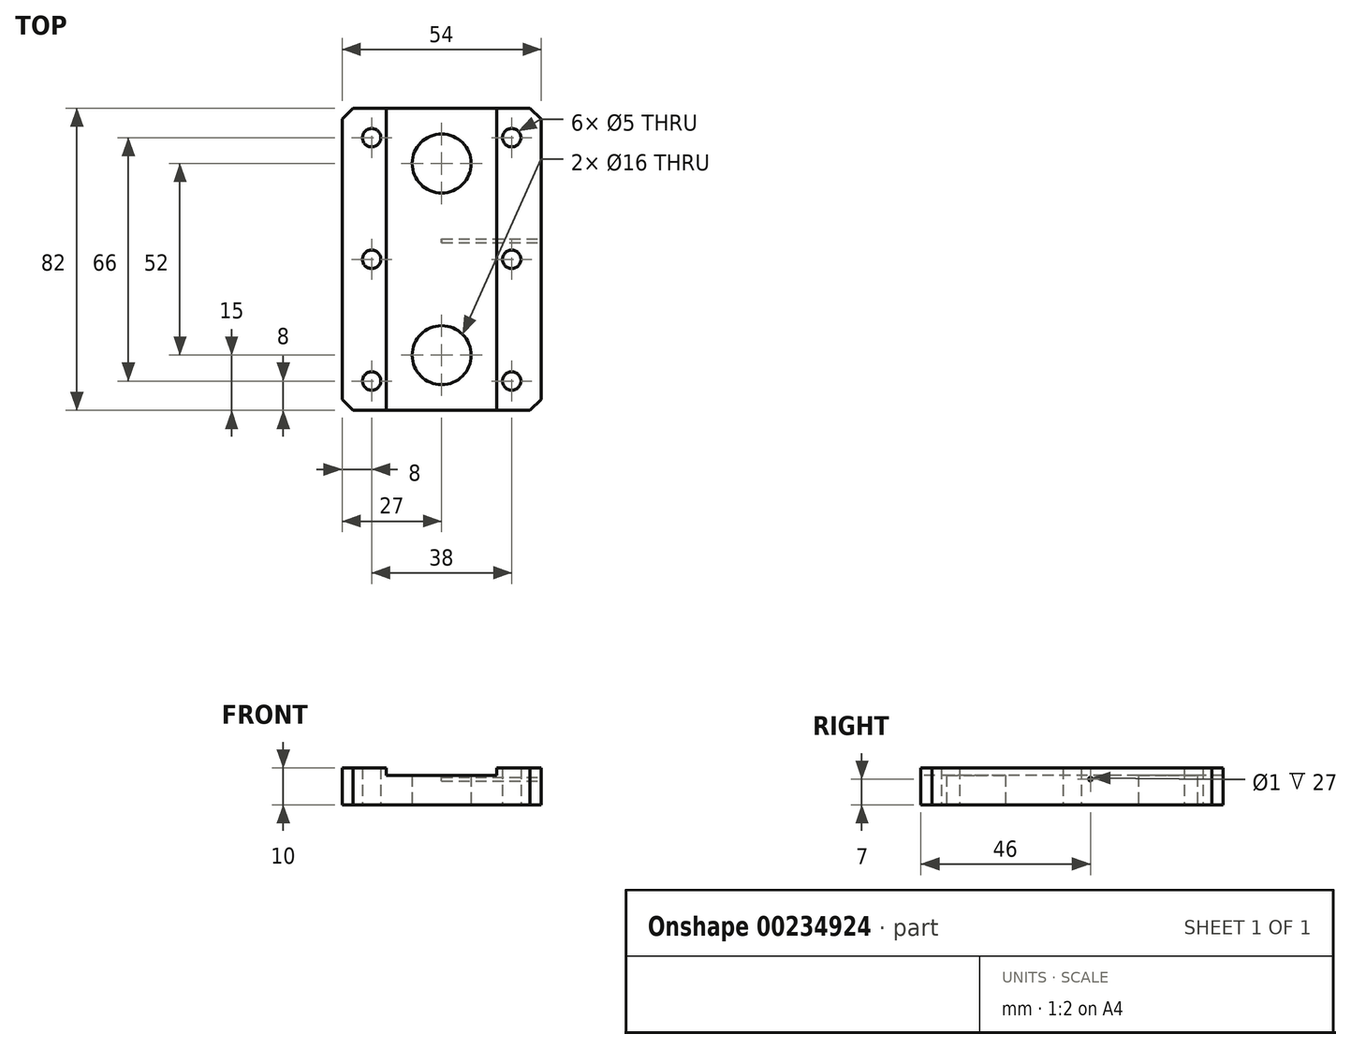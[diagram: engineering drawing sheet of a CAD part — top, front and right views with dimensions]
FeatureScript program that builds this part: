
annotation { "Feature Type Name" : "Feature", "Feature Type Description" : "" }
export const myFeature = defineFeature(function(context is Context, id is Id, definition is map)
    precondition{}
    {
        {
            var Q0;
            Q0=qCreatedBy(makeId("Top.planeOp"),FACE);
            var sketch = newSketch(context, id + "F0", { "sketchPlane" : qUnion([Q0])});
            skLineSegment(sketch, "E0.bottom", {"start": v(27, 41) * mm, "end": v(-27, 41) * mm});
            skLineSegment(sketch, "E0.top", {"start": v(27, -41) * mm, "end": v(-27, -41) * mm});
            skLineSegment(sketch, "E0.left", {"start": v(27, 41) * mm, "end": v(27, -41) * mm});
            skLineSegment(sketch, "E0.right", {"start": v(-27, 41) * mm, "end": v(-27, -41) * mm});
            skPoint(sketch, "E0.middle", {"position": v(0, 0) * mm});
            skLineSegment(sketch, "E1", {"start": v(0, 41) * mm, "end": v(0, -41) * mm, "construction": true});
            skLineSegment(sketch, "E2", {"start": v(-27, 0) * mm, "end": v(27, 0) * mm, "construction": true});
            skCircle(sketch, "E3", {"center": v(0, -26) * mm, "radius": 8 * mm});
            skCircle(sketch, "E4", {"center": v(0, 26) * mm, "radius": 8 * mm});
            skLineSegment(sketch, "E5", {"start": v(-19, 41) * mm, "end": v(-19, -41) * mm, "construction": true});
            skCircle(sketch, "E6", {"center": v(-19, 0) * mm, "radius": 2.5 * mm});
            skCircle(sketch, "E7", {"center": v(-19, 33) * mm, "radius": 2.5 * mm});
            skCircle(sketch, "E8", {"center": v(-19, -33) * mm, "radius": 2.5 * mm});
            skCircle(sketch, "E9.MirrorC", {"center": v(19, -33) * mm, "radius": 2.5 * mm});
            skCircle(sketch, "E10.MirrorC", {"center": v(19, 33) * mm, "radius": 2.5 * mm});
            skCircle(sketch, "E11.MirrorC", {"center": v(19, 0) * mm, "radius": 2.5 * mm});
            skSolve(sketch);
        }
        {
            var Q0;
            Q0=qSketchRegion(id+"F0",true);
            extrude(context, id + "F1", {"entities" : qUnion([Q0]), "depth" : 10 * mm});
        }
        {
            var Q0;
            Q0=makeQuery(id+"F1.opExtrude","SWEPT_EDGE",EDGE,{"disambiguationData":[OSD([sQuery(id+"F0.wireOp",EDGE,"E0.top"),sQuery(id+"F0.wireOp",EDGE,"E0.left")])]});
            var Q1;
            Q1=makeQuery(id+"F1.opExtrude","SWEPT_EDGE",EDGE,{"disambiguationData":[OSD([sQuery(id+"F0.wireOp",EDGE,"E0.top"),sQuery(id+"F0.wireOp",EDGE,"E0.right")])]});
            var Q2;
            Q2=makeQuery(id+"F1.opExtrude","SWEPT_EDGE",EDGE,{"disambiguationData":[OSD([sQuery(id+"F0.wireOp",EDGE,"E0.bottom"),sQuery(id+"F0.wireOp",EDGE,"E0.left")])]});
            var Q3;
            Q3=makeQuery(id+"F1.opExtrude","SWEPT_EDGE",EDGE,{"disambiguationData":[OSD([sQuery(id+"F0.wireOp",EDGE,"E0.bottom"),sQuery(id+"F0.wireOp",EDGE,"E0.right")])]});
            chamfer(context, id + "F2", {"entities" : qUnion([Q0, Q1, Q2, Q3]), "width" : 3 * mm, "tangentPropagation" : true});
        }
        {
            var Q0;
            Q0=makeQuery(id+"F1.opExtrude","CAP_FACE",FACE,{"disambiguationData":[OSD([sQuery(id+"F0.wireOp",EDGE,"E0.bottom"),sQuery(id+"F0.wireOp",EDGE,"E0.top"),sQuery(id+"F0.wireOp",EDGE,"E0.left"),sQuery(id+"F0.wireOp",EDGE,"E0.right"),sQuery(id+"F0.wireOp",EDGE,"E3"),sQuery(id+"F0.wireOp",EDGE,"E4"),sQuery(id+"F0.wireOp",EDGE,"E8"),sQuery(id+"F0.wireOp",EDGE,"E6"),sQuery(id+"F0.wireOp",EDGE,"E7"),sQuery(id+"F0.wireOp",EDGE,"E9.MirrorC"),sQuery(id+"F0.wireOp",EDGE,"E10.MirrorC"),sQuery(id+"F0.wireOp",EDGE,"E11.MirrorC")])],"isStart":false});
            var sketch = newSketch(context, id + "F3", { "sketchPlane" : qUnion([Q0])});
            skLineSegment(sketch, "E12", {"start": v(0, 41) * mm, "end": v(0, -41) * mm, "construction": true});
            skLineSegment(sketch, "E13", {"start": v(-15, 41) * mm, "end": v(-15, -41) * mm});
            skLineSegment(sketch, "E14", {"start": v(15, 41) * mm, "end": v(15, -41) * mm});
            skLineSegment(sketch, "E15", {"start": v(-15, 41) * mm, "end": v(15, 41) * mm});
            skLineSegment(sketch, "E16", {"start": v(-15, -41) * mm, "end": v(15, -41) * mm});
            skSolve(sketch);
        }
        {
            var Q0;
            Q0=qSketchRegion(id+"F3",true);
            extrude(context, id + "F4", {"entities" : qUnion([Q0]), "operationType" : NewBodyOperationType.REMOVE, "oppositeDirection" : true, "depth" : 2 * mm});
        }
        {
            var Q0;
            Q0=makeQuery(id+"F1.opExtrude","SWEPT_FACE",FACE,{"disambiguationData":[OSD([sQuery(id+"F0.wireOp",EDGE,"E0.left")])]});
            var sketch = newSketch(context, id + "F5", { "sketchPlane" : qUnion([Q0])});
            skLineSegment(sketch, "E17", {"start": v(0, 10) * mm, "end": v(0, 0) * mm, "construction": true});
            skLineSegment(sketch, "E18", {"start": v(5, 10) * mm, "end": v(5, 0) * mm, "construction": true});
            skCircle(sketch, "E19", {"center": v(5, 7) * mm, "radius": 0.5 * mm});
            skSolve(sketch);
        }
        {
            var Q0;
            Q0 = qSketchRegion(id + "F5", true);
            extrude(context, id + "F6", {"entities" : qUnion([Q0]), "operationType" : NewBodyOperationType.REMOVE, "oppositeDirection" : true, "depth" : 27 * mm, "offsetDistance" : 25 * mm});
        }
    });
